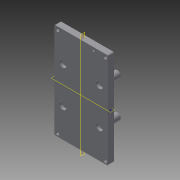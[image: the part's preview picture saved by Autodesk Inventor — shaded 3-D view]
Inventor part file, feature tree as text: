
AUTODESK INVENTOR PART (.ipt)
format: ipt  version: 2015 (Build 190159000, 159)  size: 185,344 bytes
history: native  units: mm
features: sketch x5, extrude x3, hole x3, plane x2, fillet x2, mirror x2
ambient origin geometry x8: Origin, YZ Plane, XZ Plane, XY Plane, X Axis, Y Axis, Z Axis, Center Point
bodies: Solid1 (feature_tree)
feature tree (17):
  extrude  "Extrusion1"  Depth=45.0mm
  plane  "Work Plane1"
  plane  "Work Plane2"
  hole  "Hole1"  [1 undecoded]
  fillet  "Fillet1"  Radius=2.5mm
  extrude  "Extrusion2"  Depth=1.0mm
  hole  "Hole2"  [1 undecoded]
  extrude  "Extrusion3"  Depth=10.0mm TaperAngle=0.0deg
  fillet  "Fillet2"  Radius=30.0mm
  mirror  "Mirror1"
  mirror  "Mirror2"
  hole  "Hole3"  [1 undecoded]
  sketch  "Sketch1"  dims[d0=80.0mm d1=45.0mm]
  sketch  "Sketch2"  dims[d2=5.0mm d3=0.0mm d4=2.5mm d5=2.5mm]
  sketch  "Sketch3"  dims[d6=3.1mm d7=6.0mm d8=4.0mm d9=2.0mm d10=90.0deg d11=8.0mm d12=20.594885mm d13=1.0mm]
  sketch  "Sketch4"  dims[d14=15.25mm d15=15.25mm]
  sketch  "Sketch5"  dims[d16=6.0mm d17=10.0mm d18=0.0mm d45=10.0mm d46=10.0mm d21=3.1mm d22=6.0mm d23=4.0mm d24=2.0mm d25=90.0deg d26=11.0mm d27=20.594885mm d30=30.0mm d31=2.0mm d32=6.0mm d33=4.0mm d34=2.0mm d35=90.0deg d36=10.0mm d37=20.594885mm d38=2.3mm d39=0.0mm d42=3.0mm]
note: 3 required parameter values undecoded (feature->parameter linkage not recoverable at this tier; creation-order binding heuristic only, values carry confidence <= 0.55)
